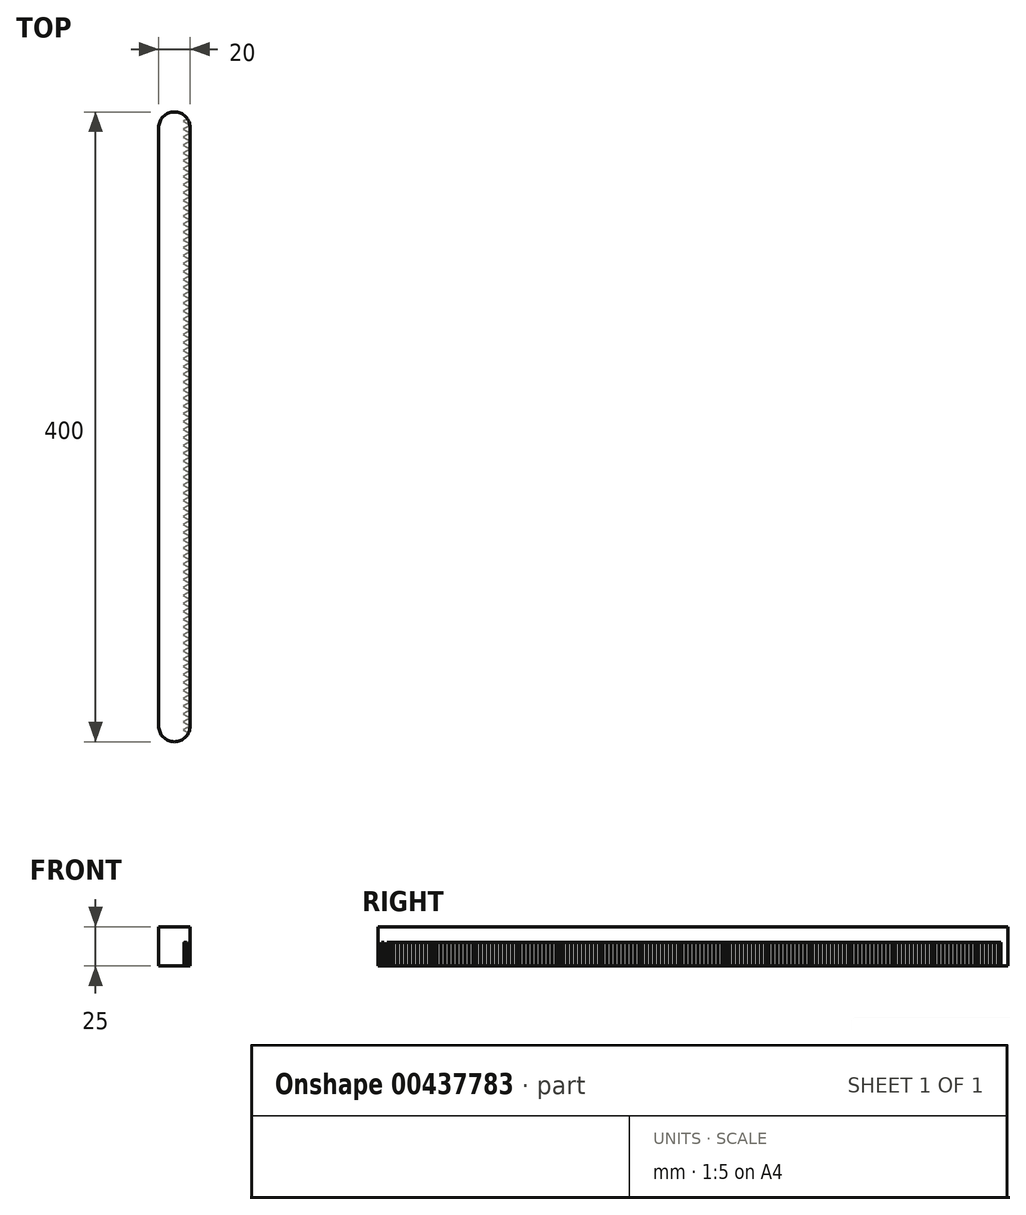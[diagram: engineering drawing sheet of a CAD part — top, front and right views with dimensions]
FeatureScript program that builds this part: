
annotation { "Feature Type Name" : "Feature", "Feature Type Description" : "" }
export const myFeature = defineFeature(function(context is Context, id is Id, definition is map)
    precondition{}
    {
        {
            var Q0;
            Q0=qCreatedBy(makeId("Top.planeOp"),FACE);
            var sketch = newSketch(context, id + "F0", { "sketchPlane" : qUnion([Q0])});
            skLineSegment(sketch, "E0.bottom", {"start": v(10, -200) * mm, "end": v(-10, -200) * mm});
            skLineSegment(sketch, "E0.top", {"start": v(10, 200) * mm, "end": v(-10, 200) * mm});
            skLineSegment(sketch, "E0.left", {"start": v(10, -200) * mm, "end": v(10, 200) * mm});
            skLineSegment(sketch, "E0.right", {"start": v(-10, -200) * mm, "end": v(-10, 200) * mm});
            skPoint(sketch, "E0.middle", {"position": v(0, 0) * mm});
            skSolve(sketch);
        }
        {
            var Q0;
            Q0 = qSketchRegion(id + "F0", true);
            extrude(context, id + "F1", {"entities" : qUnion([Q0]), "depth" : 25 * mm});
        }
        {
            var Q0;
            Q0=qCreatedBy(makeId("Top.planeOp"),FACE);
            var sketch = newSketch(context, id + "F2", { "sketchPlane" : qUnion([Q0])});
            skLineSegment(sketch, "E1", {"start": v(5.67, -197.5) * mm, "end": v(10, -200) * mm});
            skLineSegment(sketch, "E2", {"start": v(10, -200) * mm, "end": v(10, -195) * mm});
            skLineSegment(sketch, "E3", {"start": v(10, -195) * mm, "end": v(5.67, -197.5) * mm});
            skLineSegment(sketch, "E4.0.1.0", {"start": v(5.67, -192.48) * mm, "end": v(10, -194.98) * mm});
            skLineSegment(sketch, "E4.0.1.1", {"start": v(10, -194.98) * mm, "end": v(10, -189.98) * mm});
            skLineSegment(sketch, "E4.0.1.2", {"start": v(10, -189.98) * mm, "end": v(5.67, -192.48) * mm});
            skLineSegment(sketch, "E4.0.2.0", {"start": v(5.67, -187.46) * mm, "end": v(10, -189.96) * mm});
            skLineSegment(sketch, "E4.0.2.1", {"start": v(10, -189.96) * mm, "end": v(10, -184.96) * mm});
            skLineSegment(sketch, "E4.0.2.2", {"start": v(10, -184.96) * mm, "end": v(5.67, -187.46) * mm});
            skLineSegment(sketch, "E4.0.3.0", {"start": v(5.67, -182.44) * mm, "end": v(10, -184.94) * mm});
            skLineSegment(sketch, "E4.0.3.1", {"start": v(10, -184.94) * mm, "end": v(10, -179.94) * mm});
            skLineSegment(sketch, "E4.0.3.2", {"start": v(10, -179.94) * mm, "end": v(5.67, -182.44) * mm});
            skLineSegment(sketch, "E4.0.4.0", {"start": v(5.67, -177.42) * mm, "end": v(10, -179.92) * mm});
            skLineSegment(sketch, "E4.0.4.1", {"start": v(10, -179.92) * mm, "end": v(10, -174.92) * mm});
            skLineSegment(sketch, "E4.0.4.2", {"start": v(10, -174.92) * mm, "end": v(5.67, -177.42) * mm});
            skLineSegment(sketch, "E4.0.5.0", {"start": v(5.67, -172.4) * mm, "end": v(10, -174.9) * mm});
            skLineSegment(sketch, "E4.0.5.1", {"start": v(10, -174.9) * mm, "end": v(10, -169.9) * mm});
            skLineSegment(sketch, "E4.0.5.2", {"start": v(10, -169.9) * mm, "end": v(5.67, -172.4) * mm});
            skLineSegment(sketch, "E4.0.6.0", {"start": v(5.67, -167.38) * mm, "end": v(10, -169.88) * mm});
            skLineSegment(sketch, "E4.0.6.1", {"start": v(10, -169.88) * mm, "end": v(10, -164.88) * mm});
            skLineSegment(sketch, "E4.0.6.2", {"start": v(10, -164.88) * mm, "end": v(5.67, -167.38) * mm});
            skLineSegment(sketch, "E4.0.7.0", {"start": v(5.67, -162.36) * mm, "end": v(10, -164.86) * mm});
            skLineSegment(sketch, "E4.0.7.1", {"start": v(10, -164.86) * mm, "end": v(10, -159.86) * mm});
            skLineSegment(sketch, "E4.0.7.2", {"start": v(10, -159.86) * mm, "end": v(5.67, -162.36) * mm});
            skLineSegment(sketch, "E4.0.8.0", {"start": v(5.67, -157.34) * mm, "end": v(10, -159.84) * mm});
            skLineSegment(sketch, "E4.0.8.1", {"start": v(10, -159.84) * mm, "end": v(10, -154.84) * mm});
            skLineSegment(sketch, "E4.0.8.2", {"start": v(10, -154.84) * mm, "end": v(5.67, -157.34) * mm});
            skLineSegment(sketch, "E4.0.9.0", {"start": v(5.67, -152.32) * mm, "end": v(10, -154.82) * mm});
            skLineSegment(sketch, "E4.0.9.1", {"start": v(10, -154.82) * mm, "end": v(10, -149.82) * mm});
            skLineSegment(sketch, "E4.0.9.2", {"start": v(10, -149.82) * mm, "end": v(5.67, -152.32) * mm});
            skLineSegment(sketch, "E4.0.10.0", {"start": v(5.67, -147.3) * mm, "end": v(10, -149.8) * mm});
            skLineSegment(sketch, "E4.0.10.1", {"start": v(10, -149.8) * mm, "end": v(10, -144.8) * mm});
            skLineSegment(sketch, "E4.0.10.2", {"start": v(10, -144.8) * mm, "end": v(5.67, -147.3) * mm});
            skLineSegment(sketch, "E4.0.11.0", {"start": v(5.67, -142.28) * mm, "end": v(10, -144.78) * mm});
            skLineSegment(sketch, "E4.0.11.1", {"start": v(10, -144.78) * mm, "end": v(10, -139.78) * mm});
            skLineSegment(sketch, "E4.0.11.2", {"start": v(10, -139.78) * mm, "end": v(5.67, -142.28) * mm});
            skLineSegment(sketch, "E4.0.12.0", {"start": v(5.67, -137.26) * mm, "end": v(10, -139.76) * mm});
            skLineSegment(sketch, "E4.0.12.1", {"start": v(10, -139.76) * mm, "end": v(10, -134.76) * mm});
            skLineSegment(sketch, "E4.0.12.2", {"start": v(10, -134.76) * mm, "end": v(5.67, -137.26) * mm});
            skLineSegment(sketch, "E4.0.13.0", {"start": v(5.67, -132.24) * mm, "end": v(10, -134.74) * mm});
            skLineSegment(sketch, "E4.0.13.1", {"start": v(10, -134.74) * mm, "end": v(10, -129.74) * mm});
            skLineSegment(sketch, "E4.0.13.2", {"start": v(10, -129.74) * mm, "end": v(5.67, -132.24) * mm});
            skLineSegment(sketch, "E4.0.14.0", {"start": v(5.67, -127.22) * mm, "end": v(10, -129.72) * mm});
            skLineSegment(sketch, "E4.0.14.1", {"start": v(10, -129.72) * mm, "end": v(10, -124.72) * mm});
            skLineSegment(sketch, "E4.0.14.2", {"start": v(10, -124.72) * mm, "end": v(5.67, -127.22) * mm});
            skLineSegment(sketch, "E4.0.15.0", {"start": v(5.67, -122.2) * mm, "end": v(10, -124.7) * mm});
            skLineSegment(sketch, "E4.0.15.1", {"start": v(10, -124.7) * mm, "end": v(10, -119.7) * mm});
            skLineSegment(sketch, "E4.0.15.2", {"start": v(10, -119.7) * mm, "end": v(5.67, -122.2) * mm});
            skLineSegment(sketch, "E4.0.16.0", {"start": v(5.67, -117.18) * mm, "end": v(10, -119.68) * mm});
            skLineSegment(sketch, "E4.0.16.1", {"start": v(10, -119.68) * mm, "end": v(10, -114.68) * mm});
            skLineSegment(sketch, "E4.0.16.2", {"start": v(10, -114.68) * mm, "end": v(5.67, -117.18) * mm});
            skLineSegment(sketch, "E4.0.17.0", {"start": v(5.67, -112.16) * mm, "end": v(10, -114.66) * mm});
            skLineSegment(sketch, "E4.0.17.1", {"start": v(10, -114.66) * mm, "end": v(10, -109.66) * mm});
            skLineSegment(sketch, "E4.0.17.2", {"start": v(10, -109.66) * mm, "end": v(5.67, -112.16) * mm});
            skLineSegment(sketch, "E4.0.18.0", {"start": v(5.67, -107.14) * mm, "end": v(10, -109.64) * mm});
            skLineSegment(sketch, "E4.0.18.1", {"start": v(10, -109.64) * mm, "end": v(10, -104.64) * mm});
            skLineSegment(sketch, "E4.0.18.2", {"start": v(10, -104.64) * mm, "end": v(5.67, -107.14) * mm});
            skLineSegment(sketch, "E4.0.19.0", {"start": v(5.67, -102.12) * mm, "end": v(10, -104.62) * mm});
            skLineSegment(sketch, "E4.0.19.1", {"start": v(10, -104.62) * mm, "end": v(10, -99.62) * mm});
            skLineSegment(sketch, "E4.0.19.2", {"start": v(10, -99.62) * mm, "end": v(5.67, -102.12) * mm});
            skLineSegment(sketch, "E4.0.20.0", {"start": v(5.67, -97.1) * mm, "end": v(10, -99.6) * mm});
            skLineSegment(sketch, "E4.0.20.1", {"start": v(10, -99.6) * mm, "end": v(10, -94.6) * mm});
            skLineSegment(sketch, "E4.0.20.2", {"start": v(10, -94.6) * mm, "end": v(5.67, -97.1) * mm});
            skLineSegment(sketch, "E4.0.21.0", {"start": v(5.67, -92.08) * mm, "end": v(10, -94.58) * mm});
            skLineSegment(sketch, "E4.0.21.1", {"start": v(10, -94.58) * mm, "end": v(10, -89.58) * mm});
            skLineSegment(sketch, "E4.0.21.2", {"start": v(10, -89.58) * mm, "end": v(5.67, -92.08) * mm});
            skLineSegment(sketch, "E4.0.22.0", {"start": v(5.67, -87.06) * mm, "end": v(10, -89.56) * mm});
            skLineSegment(sketch, "E4.0.22.1", {"start": v(10, -89.56) * mm, "end": v(10, -84.56) * mm});
            skLineSegment(sketch, "E4.0.22.2", {"start": v(10, -84.56) * mm, "end": v(5.67, -87.06) * mm});
            skLineSegment(sketch, "E4.0.23.0", {"start": v(5.67, -82.04) * mm, "end": v(10, -84.54) * mm});
            skLineSegment(sketch, "E4.0.23.1", {"start": v(10, -84.54) * mm, "end": v(10, -79.54) * mm});
            skLineSegment(sketch, "E4.0.23.2", {"start": v(10, -79.54) * mm, "end": v(5.67, -82.04) * mm});
            skLineSegment(sketch, "E4.0.24.0", {"start": v(5.67, -77.02) * mm, "end": v(10, -79.52) * mm});
            skLineSegment(sketch, "E4.0.24.1", {"start": v(10, -79.52) * mm, "end": v(10, -74.52) * mm});
            skLineSegment(sketch, "E4.0.24.2", {"start": v(10, -74.52) * mm, "end": v(5.67, -77.02) * mm});
            skLineSegment(sketch, "E4.0.25.0", {"start": v(5.67, -72) * mm, "end": v(10, -74.5) * mm});
            skLineSegment(sketch, "E4.0.25.1", {"start": v(10, -74.5) * mm, "end": v(10, -69.5) * mm});
            skLineSegment(sketch, "E4.0.25.2", {"start": v(10, -69.5) * mm, "end": v(5.67, -72) * mm});
            skLineSegment(sketch, "E4.0.26.0", {"start": v(5.67, -66.98) * mm, "end": v(10, -69.48) * mm});
            skLineSegment(sketch, "E4.0.26.1", {"start": v(10, -69.48) * mm, "end": v(10, -64.48) * mm});
            skLineSegment(sketch, "E4.0.26.2", {"start": v(10, -64.48) * mm, "end": v(5.67, -66.98) * mm});
            skLineSegment(sketch, "E4.0.27.0", {"start": v(5.67, -61.96) * mm, "end": v(10, -64.46) * mm});
            skLineSegment(sketch, "E4.0.27.1", {"start": v(10, -64.46) * mm, "end": v(10, -59.46) * mm});
            skLineSegment(sketch, "E4.0.27.2", {"start": v(10, -59.46) * mm, "end": v(5.67, -61.96) * mm});
            skLineSegment(sketch, "E4.0.28.0", {"start": v(5.67, -56.94) * mm, "end": v(10, -59.44) * mm});
            skLineSegment(sketch, "E4.0.28.1", {"start": v(10, -59.44) * mm, "end": v(10, -54.44) * mm});
            skLineSegment(sketch, "E4.0.28.2", {"start": v(10, -54.44) * mm, "end": v(5.67, -56.94) * mm});
            skLineSegment(sketch, "E4.0.29.0", {"start": v(5.67, -51.92) * mm, "end": v(10, -54.42) * mm});
            skLineSegment(sketch, "E4.0.29.1", {"start": v(10, -54.42) * mm, "end": v(10, -49.42) * mm});
            skLineSegment(sketch, "E4.0.29.2", {"start": v(10, -49.42) * mm, "end": v(5.67, -51.92) * mm});
            skLineSegment(sketch, "E4.0.30.0", {"start": v(5.67, -46.9) * mm, "end": v(10, -49.4) * mm});
            skLineSegment(sketch, "E4.0.30.1", {"start": v(10, -49.4) * mm, "end": v(10, -44.4) * mm});
            skLineSegment(sketch, "E4.0.30.2", {"start": v(10, -44.4) * mm, "end": v(5.67, -46.9) * mm});
            skLineSegment(sketch, "E4.0.31.0", {"start": v(5.67, -41.88) * mm, "end": v(10, -44.38) * mm});
            skLineSegment(sketch, "E4.0.31.1", {"start": v(10, -44.38) * mm, "end": v(10, -39.38) * mm});
            skLineSegment(sketch, "E4.0.31.2", {"start": v(10, -39.38) * mm, "end": v(5.67, -41.88) * mm});
            skLineSegment(sketch, "E4.0.32.0", {"start": v(5.67, -36.86) * mm, "end": v(10, -39.36) * mm});
            skLineSegment(sketch, "E4.0.32.1", {"start": v(10, -39.36) * mm, "end": v(10, -34.36) * mm});
            skLineSegment(sketch, "E4.0.32.2", {"start": v(10, -34.36) * mm, "end": v(5.67, -36.86) * mm});
            skLineSegment(sketch, "E4.0.33.0", {"start": v(5.67, -31.84) * mm, "end": v(10, -34.34) * mm});
            skLineSegment(sketch, "E4.0.33.1", {"start": v(10, -34.34) * mm, "end": v(10, -29.34) * mm});
            skLineSegment(sketch, "E4.0.33.2", {"start": v(10, -29.34) * mm, "end": v(5.67, -31.84) * mm});
            skLineSegment(sketch, "E4.0.34.0", {"start": v(5.67, -26.82) * mm, "end": v(10, -29.32) * mm});
            skLineSegment(sketch, "E4.0.34.1", {"start": v(10, -29.32) * mm, "end": v(10, -24.32) * mm});
            skLineSegment(sketch, "E4.0.34.2", {"start": v(10, -24.32) * mm, "end": v(5.67, -26.82) * mm});
            skLineSegment(sketch, "E4.0.35.0", {"start": v(5.67, -21.8) * mm, "end": v(10, -24.3) * mm});
            skLineSegment(sketch, "E4.0.35.1", {"start": v(10, -24.3) * mm, "end": v(10, -19.3) * mm});
            skLineSegment(sketch, "E4.0.35.2", {"start": v(10, -19.3) * mm, "end": v(5.67, -21.8) * mm});
            skLineSegment(sketch, "E4.0.36.0", {"start": v(5.67, -16.78) * mm, "end": v(10, -19.28) * mm});
            skLineSegment(sketch, "E4.0.36.1", {"start": v(10, -19.28) * mm, "end": v(10, -14.28) * mm});
            skLineSegment(sketch, "E4.0.36.2", {"start": v(10, -14.28) * mm, "end": v(5.67, -16.78) * mm});
            skLineSegment(sketch, "E4.0.37.0", {"start": v(5.67, -11.76) * mm, "end": v(10, -14.26) * mm});
            skLineSegment(sketch, "E4.0.37.1", {"start": v(10, -14.26) * mm, "end": v(10, -9.26) * mm});
            skLineSegment(sketch, "E4.0.37.2", {"start": v(10, -9.26) * mm, "end": v(5.67, -11.76) * mm});
            skLineSegment(sketch, "E4.0.38.0", {"start": v(5.67, -6.74) * mm, "end": v(10, -9.24) * mm});
            skLineSegment(sketch, "E4.0.38.1", {"start": v(10, -9.24) * mm, "end": v(10, -4.24) * mm});
            skLineSegment(sketch, "E4.0.38.2", {"start": v(10, -4.24) * mm, "end": v(5.67, -6.74) * mm});
            skLineSegment(sketch, "E4.0.39.0", {"start": v(5.67, -1.72) * mm, "end": v(10, -4.22) * mm});
            skLineSegment(sketch, "E4.0.39.1", {"start": v(10, -4.22) * mm, "end": v(10, 0.78) * mm});
            skLineSegment(sketch, "E4.0.39.2", {"start": v(10, 0.78) * mm, "end": v(5.67, -1.72) * mm});
            skLineSegment(sketch, "E4.0.40.0", {"start": v(5.67, 3.3) * mm, "end": v(10, 0.8) * mm});
            skLineSegment(sketch, "E4.0.40.1", {"start": v(10, 0.8) * mm, "end": v(10, 5.8) * mm});
            skLineSegment(sketch, "E4.0.40.2", {"start": v(10, 5.8) * mm, "end": v(5.67, 3.3) * mm});
            skLineSegment(sketch, "E4.0.41.0", {"start": v(5.67, 8.32) * mm, "end": v(10, 5.82) * mm});
            skLineSegment(sketch, "E4.0.41.1", {"start": v(10, 5.82) * mm, "end": v(10, 10.82) * mm});
            skLineSegment(sketch, "E4.0.41.2", {"start": v(10, 10.82) * mm, "end": v(5.67, 8.32) * mm});
            skLineSegment(sketch, "E4.0.42.0", {"start": v(5.67, 13.34) * mm, "end": v(10, 10.84) * mm});
            skLineSegment(sketch, "E4.0.42.1", {"start": v(10, 10.84) * mm, "end": v(10, 15.84) * mm});
            skLineSegment(sketch, "E4.0.42.2", {"start": v(10, 15.84) * mm, "end": v(5.67, 13.34) * mm});
            skLineSegment(sketch, "E4.0.43.0", {"start": v(5.67, 18.36) * mm, "end": v(10, 15.86) * mm});
            skLineSegment(sketch, "E4.0.43.1", {"start": v(10, 15.86) * mm, "end": v(10, 20.86) * mm});
            skLineSegment(sketch, "E4.0.43.2", {"start": v(10, 20.86) * mm, "end": v(5.67, 18.36) * mm});
            skLineSegment(sketch, "E4.0.44.0", {"start": v(5.67, 23.38) * mm, "end": v(10, 20.88) * mm});
            skLineSegment(sketch, "E4.0.44.1", {"start": v(10, 20.88) * mm, "end": v(10, 25.88) * mm});
            skLineSegment(sketch, "E4.0.44.2", {"start": v(10, 25.88) * mm, "end": v(5.67, 23.38) * mm});
            skLineSegment(sketch, "E4.0.45.0", {"start": v(5.67, 28.4) * mm, "end": v(10, 25.9) * mm});
            skLineSegment(sketch, "E4.0.45.1", {"start": v(10, 25.9) * mm, "end": v(10, 30.9) * mm});
            skLineSegment(sketch, "E4.0.45.2", {"start": v(10, 30.9) * mm, "end": v(5.67, 28.4) * mm});
            skLineSegment(sketch, "E4.0.46.0", {"start": v(5.67, 33.42) * mm, "end": v(10, 30.92) * mm});
            skLineSegment(sketch, "E4.0.46.1", {"start": v(10, 30.92) * mm, "end": v(10, 35.92) * mm});
            skLineSegment(sketch, "E4.0.46.2", {"start": v(10, 35.92) * mm, "end": v(5.67, 33.42) * mm});
            skLineSegment(sketch, "E4.0.47.0", {"start": v(5.67, 38.44) * mm, "end": v(10, 35.94) * mm});
            skLineSegment(sketch, "E4.0.47.1", {"start": v(10, 35.94) * mm, "end": v(10, 40.94) * mm});
            skLineSegment(sketch, "E4.0.47.2", {"start": v(10, 40.94) * mm, "end": v(5.67, 38.44) * mm});
            skLineSegment(sketch, "E4.0.48.0", {"start": v(5.67, 43.46) * mm, "end": v(10, 40.96) * mm});
            skLineSegment(sketch, "E4.0.48.1", {"start": v(10, 40.96) * mm, "end": v(10, 45.96) * mm});
            skLineSegment(sketch, "E4.0.48.2", {"start": v(10, 45.96) * mm, "end": v(5.67, 43.46) * mm});
            skLineSegment(sketch, "E4.0.49.0", {"start": v(5.67, 48.48) * mm, "end": v(10, 45.98) * mm});
            skLineSegment(sketch, "E4.0.49.1", {"start": v(10, 45.98) * mm, "end": v(10, 50.98) * mm});
            skLineSegment(sketch, "E4.0.49.2", {"start": v(10, 50.98) * mm, "end": v(5.67, 48.48) * mm});
            skLineSegment(sketch, "E4.0.50.0", {"start": v(5.67, 53.5) * mm, "end": v(10, 51) * mm});
            skLineSegment(sketch, "E4.0.50.1", {"start": v(10, 51) * mm, "end": v(10, 56) * mm});
            skLineSegment(sketch, "E4.0.50.2", {"start": v(10, 56) * mm, "end": v(5.67, 53.5) * mm});
            skLineSegment(sketch, "E4.0.51.0", {"start": v(5.67, 58.52) * mm, "end": v(10, 56.02) * mm});
            skLineSegment(sketch, "E4.0.51.1", {"start": v(10, 56.02) * mm, "end": v(10, 61.02) * mm});
            skLineSegment(sketch, "E4.0.51.2", {"start": v(10, 61.02) * mm, "end": v(5.67, 58.52) * mm});
            skLineSegment(sketch, "E4.0.52.0", {"start": v(5.67, 63.54) * mm, "end": v(10, 61.04) * mm});
            skLineSegment(sketch, "E4.0.52.1", {"start": v(10, 61.04) * mm, "end": v(10, 66.04) * mm});
            skLineSegment(sketch, "E4.0.52.2", {"start": v(10, 66.04) * mm, "end": v(5.67, 63.54) * mm});
            skLineSegment(sketch, "E4.0.53.0", {"start": v(5.67, 68.56) * mm, "end": v(10, 66.06) * mm});
            skLineSegment(sketch, "E4.0.53.1", {"start": v(10, 66.06) * mm, "end": v(10, 71.06) * mm});
            skLineSegment(sketch, "E4.0.53.2", {"start": v(10, 71.06) * mm, "end": v(5.67, 68.56) * mm});
            skLineSegment(sketch, "E4.0.54.0", {"start": v(5.67, 73.58) * mm, "end": v(10, 71.08) * mm});
            skLineSegment(sketch, "E4.0.54.1", {"start": v(10, 71.08) * mm, "end": v(10, 76.08) * mm});
            skLineSegment(sketch, "E4.0.54.2", {"start": v(10, 76.08) * mm, "end": v(5.67, 73.58) * mm});
            skLineSegment(sketch, "E4.0.55.0", {"start": v(5.67, 78.6) * mm, "end": v(10, 76.1) * mm});
            skLineSegment(sketch, "E4.0.55.1", {"start": v(10, 76.1) * mm, "end": v(10, 81.1) * mm});
            skLineSegment(sketch, "E4.0.55.2", {"start": v(10, 81.1) * mm, "end": v(5.67, 78.6) * mm});
            skLineSegment(sketch, "E4.0.56.0", {"start": v(5.67, 83.62) * mm, "end": v(10, 81.12) * mm});
            skLineSegment(sketch, "E4.0.56.1", {"start": v(10, 81.12) * mm, "end": v(10, 86.12) * mm});
            skLineSegment(sketch, "E4.0.56.2", {"start": v(10, 86.12) * mm, "end": v(5.67, 83.62) * mm});
            skLineSegment(sketch, "E4.0.57.0", {"start": v(5.67, 88.64) * mm, "end": v(10, 86.14) * mm});
            skLineSegment(sketch, "E4.0.57.1", {"start": v(10, 86.14) * mm, "end": v(10, 91.14) * mm});
            skLineSegment(sketch, "E4.0.57.2", {"start": v(10, 91.14) * mm, "end": v(5.67, 88.64) * mm});
            skLineSegment(sketch, "E4.0.58.0", {"start": v(5.67, 93.66) * mm, "end": v(10, 91.16) * mm});
            skLineSegment(sketch, "E4.0.58.1", {"start": v(10, 91.16) * mm, "end": v(10, 96.16) * mm});
            skLineSegment(sketch, "E4.0.58.2", {"start": v(10, 96.16) * mm, "end": v(5.67, 93.66) * mm});
            skLineSegment(sketch, "E4.0.59.0", {"start": v(5.67, 98.68) * mm, "end": v(10, 96.18) * mm});
            skLineSegment(sketch, "E4.0.59.1", {"start": v(10, 96.18) * mm, "end": v(10, 101.18) * mm});
            skLineSegment(sketch, "E4.0.59.2", {"start": v(10, 101.18) * mm, "end": v(5.67, 98.68) * mm});
            skLineSegment(sketch, "E4.0.60.0", {"start": v(5.67, 103.7) * mm, "end": v(10, 101.2) * mm});
            skLineSegment(sketch, "E4.0.60.1", {"start": v(10, 101.2) * mm, "end": v(10, 106.2) * mm});
            skLineSegment(sketch, "E4.0.60.2", {"start": v(10, 106.2) * mm, "end": v(5.67, 103.7) * mm});
            skLineSegment(sketch, "E4.0.61.0", {"start": v(5.67, 108.72) * mm, "end": v(10, 106.22) * mm});
            skLineSegment(sketch, "E4.0.61.1", {"start": v(10, 106.22) * mm, "end": v(10, 111.22) * mm});
            skLineSegment(sketch, "E4.0.61.2", {"start": v(10, 111.22) * mm, "end": v(5.67, 108.72) * mm});
            skLineSegment(sketch, "E4.0.62.0", {"start": v(5.67, 113.74) * mm, "end": v(10, 111.24) * mm});
            skLineSegment(sketch, "E4.0.62.1", {"start": v(10, 111.24) * mm, "end": v(10, 116.24) * mm});
            skLineSegment(sketch, "E4.0.62.2", {"start": v(10, 116.24) * mm, "end": v(5.67, 113.74) * mm});
            skLineSegment(sketch, "E4.0.63.0", {"start": v(5.67, 118.76) * mm, "end": v(10, 116.26) * mm});
            skLineSegment(sketch, "E4.0.63.1", {"start": v(10, 116.26) * mm, "end": v(10, 121.26) * mm});
            skLineSegment(sketch, "E4.0.63.2", {"start": v(10, 121.26) * mm, "end": v(5.67, 118.76) * mm});
            skLineSegment(sketch, "E4.0.64.0", {"start": v(5.67, 123.78) * mm, "end": v(10, 121.28) * mm});
            skLineSegment(sketch, "E4.0.64.1", {"start": v(10, 121.28) * mm, "end": v(10, 126.28) * mm});
            skLineSegment(sketch, "E4.0.64.2", {"start": v(10, 126.28) * mm, "end": v(5.67, 123.78) * mm});
            skLineSegment(sketch, "E4.0.65.0", {"start": v(5.67, 128.8) * mm, "end": v(10, 126.3) * mm});
            skLineSegment(sketch, "E4.0.65.1", {"start": v(10, 126.3) * mm, "end": v(10, 131.3) * mm});
            skLineSegment(sketch, "E4.0.65.2", {"start": v(10, 131.3) * mm, "end": v(5.67, 128.8) * mm});
            skLineSegment(sketch, "E4.0.66.0", {"start": v(5.67, 133.82) * mm, "end": v(10, 131.32) * mm});
            skLineSegment(sketch, "E4.0.66.1", {"start": v(10, 131.32) * mm, "end": v(10, 136.32) * mm});
            skLineSegment(sketch, "E4.0.66.2", {"start": v(10, 136.32) * mm, "end": v(5.67, 133.82) * mm});
            skLineSegment(sketch, "E4.0.67.0", {"start": v(5.67, 138.84) * mm, "end": v(10, 136.34) * mm});
            skLineSegment(sketch, "E4.0.67.1", {"start": v(10, 136.34) * mm, "end": v(10, 141.34) * mm});
            skLineSegment(sketch, "E4.0.67.2", {"start": v(10, 141.34) * mm, "end": v(5.67, 138.84) * mm});
            skLineSegment(sketch, "E4.0.68.0", {"start": v(5.67, 143.86) * mm, "end": v(10, 141.36) * mm});
            skLineSegment(sketch, "E4.0.68.1", {"start": v(10, 141.36) * mm, "end": v(10, 146.36) * mm});
            skLineSegment(sketch, "E4.0.68.2", {"start": v(10, 146.36) * mm, "end": v(5.67, 143.86) * mm});
            skLineSegment(sketch, "E4.0.69.0", {"start": v(5.67, 148.88) * mm, "end": v(10, 146.38) * mm});
            skLineSegment(sketch, "E4.0.69.1", {"start": v(10, 146.38) * mm, "end": v(10, 151.38) * mm});
            skLineSegment(sketch, "E4.0.69.2", {"start": v(10, 151.38) * mm, "end": v(5.67, 148.88) * mm});
            skLineSegment(sketch, "E4.0.70.0", {"start": v(5.67, 153.9) * mm, "end": v(10, 151.4) * mm});
            skLineSegment(sketch, "E4.0.70.1", {"start": v(10, 151.4) * mm, "end": v(10, 156.4) * mm});
            skLineSegment(sketch, "E4.0.70.2", {"start": v(10, 156.4) * mm, "end": v(5.67, 153.9) * mm});
            skLineSegment(sketch, "E4.0.71.0", {"start": v(5.67, 158.92) * mm, "end": v(10, 156.42) * mm});
            skLineSegment(sketch, "E4.0.71.1", {"start": v(10, 156.42) * mm, "end": v(10, 161.42) * mm});
            skLineSegment(sketch, "E4.0.71.2", {"start": v(10, 161.42) * mm, "end": v(5.67, 158.92) * mm});
            skLineSegment(sketch, "E4.0.72.0", {"start": v(5.67, 163.94) * mm, "end": v(10, 161.44) * mm});
            skLineSegment(sketch, "E4.0.72.1", {"start": v(10, 161.44) * mm, "end": v(10, 166.44) * mm});
            skLineSegment(sketch, "E4.0.72.2", {"start": v(10, 166.44) * mm, "end": v(5.67, 163.94) * mm});
            skLineSegment(sketch, "E4.0.73.0", {"start": v(5.67, 168.96) * mm, "end": v(10, 166.46) * mm});
            skLineSegment(sketch, "E4.0.73.1", {"start": v(10, 166.46) * mm, "end": v(10, 171.46) * mm});
            skLineSegment(sketch, "E4.0.73.2", {"start": v(10, 171.46) * mm, "end": v(5.67, 168.96) * mm});
            skLineSegment(sketch, "E4.0.74.0", {"start": v(5.67, 173.98) * mm, "end": v(10, 171.48) * mm});
            skLineSegment(sketch, "E4.0.74.1", {"start": v(10, 171.48) * mm, "end": v(10, 176.48) * mm});
            skLineSegment(sketch, "E4.0.74.2", {"start": v(10, 176.48) * mm, "end": v(5.67, 173.98) * mm});
            skLineSegment(sketch, "E4.0.75.0", {"start": v(5.67, 179) * mm, "end": v(10, 176.5) * mm});
            skLineSegment(sketch, "E4.0.75.1", {"start": v(10, 176.5) * mm, "end": v(10, 181.5) * mm});
            skLineSegment(sketch, "E4.0.75.2", {"start": v(10, 181.5) * mm, "end": v(5.67, 179) * mm});
            skLineSegment(sketch, "E4.0.76.0", {"start": v(5.67, 184.02) * mm, "end": v(10, 181.52) * mm});
            skLineSegment(sketch, "E4.0.76.1", {"start": v(10, 181.52) * mm, "end": v(10, 186.52) * mm});
            skLineSegment(sketch, "E4.0.76.2", {"start": v(10, 186.52) * mm, "end": v(5.67, 184.02) * mm});
            skLineSegment(sketch, "E4.0.77.0", {"start": v(5.67, 189.04) * mm, "end": v(10, 186.54) * mm});
            skLineSegment(sketch, "E4.0.77.1", {"start": v(10, 186.54) * mm, "end": v(10, 191.54) * mm});
            skLineSegment(sketch, "E4.0.77.2", {"start": v(10, 191.54) * mm, "end": v(5.67, 189.04) * mm});
            skLineSegment(sketch, "E4.0.78.0", {"start": v(5.67, 194.06) * mm, "end": v(10, 191.56) * mm});
            skLineSegment(sketch, "E4.0.78.1", {"start": v(10, 191.56) * mm, "end": v(10, 196.56) * mm});
            skLineSegment(sketch, "E4.0.78.2", {"start": v(10, 196.56) * mm, "end": v(5.67, 194.06) * mm});
            skLineSegment(sketch, "E4.0.79.0", {"start": v(5.67, 199.08) * mm, "end": v(10, 196.58) * mm});
            skLineSegment(sketch, "E4.0.79.1", {"start": v(10, 196.58) * mm, "end": v(10, 201.58) * mm});
            skLineSegment(sketch, "E4.0.79.2", {"start": v(10, 201.58) * mm, "end": v(5.67, 199.08) * mm});
            skLineSegment(sketch, "E4.0.80.0", {"start": v(5.67, 204.1) * mm, "end": v(10, 201.6) * mm});
            skLineSegment(sketch, "E4.0.80.1", {"start": v(10, 201.6) * mm, "end": v(10, 206.6) * mm});
            skLineSegment(sketch, "E4.0.80.2", {"start": v(10, 206.6) * mm, "end": v(5.67, 204.1) * mm});
            skLineSegment(sketch, "E4.0.81.0", {"start": v(5.67, 209.12) * mm, "end": v(10, 206.62) * mm});
            skLineSegment(sketch, "E4.0.81.1", {"start": v(10, 206.62) * mm, "end": v(10, 211.62) * mm});
            skLineSegment(sketch, "E4.0.81.2", {"start": v(10, 211.62) * mm, "end": v(5.67, 209.12) * mm});
            skLineSegment(sketch, "E4.0.82.0", {"start": v(5.67, 214.14) * mm, "end": v(10, 211.64) * mm});
            skLineSegment(sketch, "E4.0.82.1", {"start": v(10, 211.64) * mm, "end": v(10, 216.64) * mm});
            skLineSegment(sketch, "E4.0.82.2", {"start": v(10, 216.64) * mm, "end": v(5.67, 214.14) * mm});
            skLineSegment(sketch, "E4.0.83.0", {"start": v(5.67, 219.16) * mm, "end": v(10, 216.66) * mm});
            skLineSegment(sketch, "E4.0.83.1", {"start": v(10, 216.66) * mm, "end": v(10, 221.66) * mm});
            skLineSegment(sketch, "E4.0.83.2", {"start": v(10, 221.66) * mm, "end": v(5.67, 219.16) * mm});
            skLineSegment(sketch, "E4.0.84.0", {"start": v(5.67, 224.18) * mm, "end": v(10, 221.68) * mm});
            skLineSegment(sketch, "E4.0.84.1", {"start": v(10, 221.68) * mm, "end": v(10, 226.68) * mm});
            skLineSegment(sketch, "E4.0.84.2", {"start": v(10, 226.68) * mm, "end": v(5.67, 224.18) * mm});
            skLineSegment(sketch, "E4.0.85.0", {"start": v(5.67, 229.2) * mm, "end": v(10, 226.7) * mm});
            skLineSegment(sketch, "E4.0.85.1", {"start": v(10, 226.7) * mm, "end": v(10, 231.7) * mm});
            skLineSegment(sketch, "E4.0.85.2", {"start": v(10, 231.7) * mm, "end": v(5.67, 229.2) * mm});
            skLineSegment(sketch, "E4.0.86.0", {"start": v(5.67, 234.22) * mm, "end": v(10, 231.72) * mm});
            skLineSegment(sketch, "E4.0.86.1", {"start": v(10, 231.72) * mm, "end": v(10, 236.72) * mm});
            skLineSegment(sketch, "E4.0.86.2", {"start": v(10, 236.72) * mm, "end": v(5.67, 234.22) * mm});
            skLineSegment(sketch, "E4.0.87.0", {"start": v(5.67, 239.24) * mm, "end": v(10, 236.74) * mm});
            skLineSegment(sketch, "E4.0.87.1", {"start": v(10, 236.74) * mm, "end": v(10, 241.74) * mm});
            skLineSegment(sketch, "E4.0.87.2", {"start": v(10, 241.74) * mm, "end": v(5.67, 239.24) * mm});
            skLineSegment(sketch, "E4.0.88.0", {"start": v(5.67, 244.26) * mm, "end": v(10, 241.76) * mm});
            skLineSegment(sketch, "E4.0.88.1", {"start": v(10, 241.76) * mm, "end": v(10, 246.76) * mm});
            skLineSegment(sketch, "E4.0.88.2", {"start": v(10, 246.76) * mm, "end": v(5.67, 244.26) * mm});
            skLineSegment(sketch, "E4.0.89.0", {"start": v(5.67, 249.28) * mm, "end": v(10, 246.78) * mm});
            skLineSegment(sketch, "E4.0.89.1", {"start": v(10, 246.78) * mm, "end": v(10, 251.78) * mm});
            skLineSegment(sketch, "E4.0.89.2", {"start": v(10, 251.78) * mm, "end": v(5.67, 249.28) * mm});
            skLineSegment(sketch, "E4.0.90.0", {"start": v(5.67, 254.3) * mm, "end": v(10, 251.8) * mm});
            skLineSegment(sketch, "E4.0.90.1", {"start": v(10, 251.8) * mm, "end": v(10, 256.8) * mm});
            skLineSegment(sketch, "E4.0.90.2", {"start": v(10, 256.8) * mm, "end": v(5.67, 254.3) * mm});
            skLineSegment(sketch, "E4.0.91.0", {"start": v(5.67, 259.32) * mm, "end": v(10, 256.82) * mm});
            skLineSegment(sketch, "E4.0.91.1", {"start": v(10, 256.82) * mm, "end": v(10, 261.82) * mm});
            skLineSegment(sketch, "E4.0.91.2", {"start": v(10, 261.82) * mm, "end": v(5.67, 259.32) * mm});
            skLineSegment(sketch, "E4.0.92.0", {"start": v(5.67, 264.34) * mm, "end": v(10, 261.84) * mm});
            skLineSegment(sketch, "E4.0.92.1", {"start": v(10, 261.84) * mm, "end": v(10, 266.84) * mm});
            skLineSegment(sketch, "E4.0.92.2", {"start": v(10, 266.84) * mm, "end": v(5.67, 264.34) * mm});
            skLineSegment(sketch, "E4.0.93.0", {"start": v(5.67, 269.36) * mm, "end": v(10, 266.86) * mm});
            skLineSegment(sketch, "E4.0.93.1", {"start": v(10, 266.86) * mm, "end": v(10, 271.86) * mm});
            skLineSegment(sketch, "E4.0.93.2", {"start": v(10, 271.86) * mm, "end": v(5.67, 269.36) * mm});
            skLineSegment(sketch, "E4.0.94.0", {"start": v(5.67, 274.38) * mm, "end": v(10, 271.88) * mm});
            skLineSegment(sketch, "E4.0.94.1", {"start": v(10, 271.88) * mm, "end": v(10, 276.88) * mm});
            skLineSegment(sketch, "E4.0.94.2", {"start": v(10, 276.88) * mm, "end": v(5.67, 274.38) * mm});
            skLineSegment(sketch, "E4.0.95.0", {"start": v(5.67, 279.4) * mm, "end": v(10, 276.9) * mm});
            skLineSegment(sketch, "E4.0.95.1", {"start": v(10, 276.9) * mm, "end": v(10, 281.9) * mm});
            skLineSegment(sketch, "E4.0.95.2", {"start": v(10, 281.9) * mm, "end": v(5.67, 279.4) * mm});
            skLineSegment(sketch, "E4.0.96.0", {"start": v(5.67, 284.42) * mm, "end": v(10, 281.92) * mm});
            skLineSegment(sketch, "E4.0.96.1", {"start": v(10, 281.92) * mm, "end": v(10, 286.92) * mm});
            skLineSegment(sketch, "E4.0.96.2", {"start": v(10, 286.92) * mm, "end": v(5.67, 284.42) * mm});
            skLineSegment(sketch, "E4.0.97.0", {"start": v(5.67, 289.44) * mm, "end": v(10, 286.94) * mm});
            skLineSegment(sketch, "E4.0.97.1", {"start": v(10, 286.94) * mm, "end": v(10, 291.94) * mm});
            skLineSegment(sketch, "E4.0.97.2", {"start": v(10, 291.94) * mm, "end": v(5.67, 289.44) * mm});
            skLineSegment(sketch, "E4.0.98.0", {"start": v(5.67, 294.46) * mm, "end": v(10, 291.96) * mm});
            skLineSegment(sketch, "E4.0.98.1", {"start": v(10, 291.96) * mm, "end": v(10, 296.96) * mm});
            skLineSegment(sketch, "E4.0.98.2", {"start": v(10, 296.96) * mm, "end": v(5.67, 294.46) * mm});
            skLineSegment(sketch, "E4.0.99.0", {"start": v(5.67, 299.48) * mm, "end": v(10, 296.98) * mm});
            skLineSegment(sketch, "E4.0.99.1", {"start": v(10, 296.98) * mm, "end": v(10, 301.98) * mm});
            skLineSegment(sketch, "E4.0.99.2", {"start": v(10, 301.98) * mm, "end": v(5.67, 299.48) * mm});
            skLineSegment(sketch, "E4.direction1", {"start": v(5.67, -197.5) * mm, "end": v(30.67, -197.5) * mm, "construction": true});
            skLineSegment(sketch, "E4.direction2", {"start": v(5.67, -197.5) * mm, "end": v(5.67, -192.48) * mm, "construction": true});
            skSolve(sketch);
        }
        {
            var Q0;
            Q0=makeQuery(id+"F1.opExtrude","SWEPT_EDGE",EDGE,{"disambiguationData":[OSD([sQuery(id+"F0.wireOp",EDGE,"E0.bottom"),sQuery(id+"F0.wireOp",EDGE,"E0.left")])]});
            var Q1;
            Q1=makeQuery(id+"F1.opExtrude","SWEPT_EDGE",EDGE,{"disambiguationData":[OSD([sQuery(id+"F0.wireOp",EDGE,"E0.bottom"),sQuery(id+"F0.wireOp",EDGE,"E0.right")])]});
            var Q2;
            Q2=makeQuery(id+"F1.opExtrude","SWEPT_EDGE",EDGE,{"disambiguationData":[OSD([sQuery(id+"F0.wireOp",EDGE,"E0.top"),sQuery(id+"F0.wireOp",EDGE,"E0.left")])]});
            var Q3;
            Q3=makeQuery(id+"F1.opExtrude","SWEPT_EDGE",EDGE,{"disambiguationData":[OSD([sQuery(id+"F0.wireOp",EDGE,"E0.top"),sQuery(id+"F0.wireOp",EDGE,"E0.right")])]});
            fillet(context, id + "F3", {"entities" : qUnion([Q0, Q1, Q2, Q3]), "radius" : 10 * mm, "tangentPropagation" : true, "allowEdgeOverflow" : false});
        }
        {
            var Q0;
            Q0 = qSketchRegion(id + "F2", true);
            extrude(context, id + "F4", {"entities" : qUnion([Q0]), "operationType" : NewBodyOperationType.REMOVE, "depth" : 15 * mm});
        }
    });
